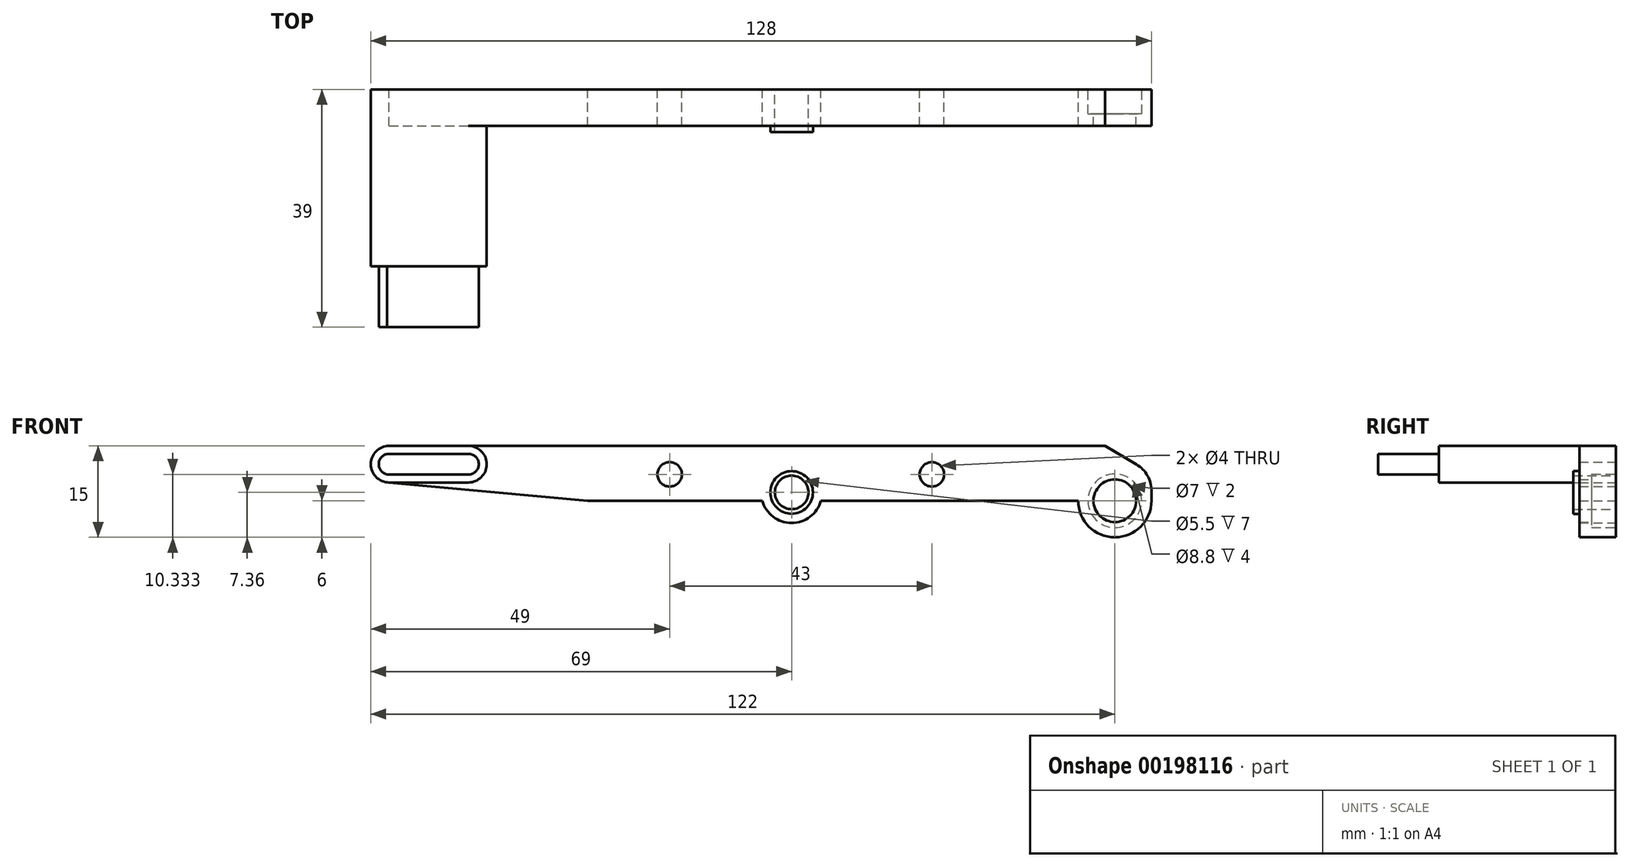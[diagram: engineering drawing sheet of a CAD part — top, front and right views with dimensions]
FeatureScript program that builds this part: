
annotation { "Feature Type Name" : "Feature", "Feature Type Description" : "" }
export const myFeature = defineFeature(function(context is Context, id is Id, definition is map)
    precondition{}
    {
        {
            var Q0;
            Q0=qCreatedBy(makeId("Front.planeOp"),FACE);
            var sketch = newSketch(context, id + "F0", { "sketchPlane" : qUnion([Q0])});
            skLineSegment(sketch, "E0.bottom", {"start": v(32.55, 0) * mm, "end": v(125, 0) * mm});
            skLineSegment(sketch, "E0.top", {"start": v(0, 9) * mm, "end": v(117.37, 9) * mm});
            skLineSegment(sketch, "E0.left", {"start": v(0, 3) * mm, "end": v(0, 9) * mm});
            skLineSegment(sketch, "E0.right", {"start": v(125, 0) * mm, "end": v(125, 1.64) * mm});
            skArc(sketch, "E1", {"start": v(113, 0) * mm, "mid": v(119, -6) * mm, "end": v(125, 0) * mm});
            skCircle(sketch, "E2", {"center": v(119, 0) * mm, "radius": 3.5 * mm});
            skArc(sketch, "E3", {"start": v(61.19, 0) * mm, "mid": v(66, -3.64) * mm, "end": v(70.81, 0) * mm});
            skCircle(sketch, "E4", {"center": v(66, 1.36) * mm, "radius": 2.75 * mm});
            skCircle(sketch, "E5", {"center": v(89, 4.33) * mm, "radius": 2 * mm});
            skCircle(sketch, "E6", {"center": v(46, 4.33) * mm, "radius": 2 * mm});
            skLineSegment(sketch, "E7", {"start": v(117.37, 9) * mm, "end": v(122.54, 5.95) * mm});
            skPoint(sketch, "E8.orphan", {"position": v(125, 9) * mm});
            skLineSegment(sketch, "E9", {"start": v(0, 3) * mm, "end": v(32.55, 0) * mm});
            skPoint(sketch, "E10.orphan", {"position": v(0, 0) * mm});
            skPoint(sketch, "E11.visualSharp", {"position": v(125, 4.5) * mm});
            skArc(sketch, "E11.filletArc", {"start": v(125, 1.64) * mm, "mid": v(124.34, 4.12) * mm, "end": v(122.54, 5.95) * mm});
            skArc(sketch, "E12", {"start": v(0, 9) * mm, "mid": v(-3, 6) * mm, "end": v(0, 3) * mm});
            skSolve(sketch);
        }
        {
            var Q0;
            Q0 = qSketchRegion(id + "F0", true);
            extrude(context, id + "F1", {"entities" : qUnion([Q0]), "depth" : 6 * mm});
        }
        {
            var Q0;
            Q0=makeQuery(id+"F1.opExtrude","CAP_FACE",FACE,{"disambiguationData":[OSD([sQuery(id+"F0.wireOp",EDGE,"E0.bottom"),sQuery(id+"F0.wireOp",EDGE,"E0.top"),sQuery(id+"F0.wireOp",EDGE,"E0.right"),sQuery(id+"F0.wireOp",EDGE,"E1"),sQuery(id+"F0.wireOp",EDGE,"E2"),sQuery(id+"F0.wireOp",EDGE,"E3"),sQuery(id+"F0.wireOp",EDGE,"E4"),sQuery(id+"F0.wireOp",EDGE,"E5"),sQuery(id+"F0.wireOp",EDGE,"E6"),sQuery(id+"F0.wireOp",EDGE,"E7"),sQuery(id+"F0.wireOp",EDGE,"E9"),sQuery(id+"F0.wireOp",EDGE,"E11.filletArc"),sQuery(id+"F0.wireOp",EDGE,"E12")])],"isStart":true});
            var sketch = newSketch(context, id + "F2", { "sketchPlane" : qUnion([Q0])});
            skCircle(sketch, "E13", {"center": v(-119, 0) * mm, "radius": 4.4 * mm});
            skSolve(sketch);
        }
        {
            var Q0;
            Q0 = qSketchRegion(id + "F2", true);
            extrude(context, id + "F3", {"entities" : qUnion([Q0]), "operationType" : NewBodyOperationType.REMOVE, "oppositeDirection" : true, "depth" : 4 * mm});
        }
        {
            var Q0;
            Q0=makeQuery(id+"F1.opExtrude","CAP_FACE",FACE,{"disambiguationData":[OSD([sQuery(id+"F0.wireOp",EDGE,"E0.bottom"),sQuery(id+"F0.wireOp",EDGE,"E0.top"),sQuery(id+"F0.wireOp",EDGE,"E0.right"),sQuery(id+"F0.wireOp",EDGE,"E1"),sQuery(id+"F0.wireOp",EDGE,"E2"),sQuery(id+"F0.wireOp",EDGE,"E3"),sQuery(id+"F0.wireOp",EDGE,"E4"),sQuery(id+"F0.wireOp",EDGE,"E5"),sQuery(id+"F0.wireOp",EDGE,"E6"),sQuery(id+"F0.wireOp",EDGE,"E7"),sQuery(id+"F0.wireOp",EDGE,"E9"),sQuery(id+"F0.wireOp",EDGE,"E11.filletArc"),sQuery(id+"F0.wireOp",EDGE,"E12")])],"isStart":true});
            var sketch = newSketch(context, id + "F4", { "sketchPlane" : qUnion([Q0])});
            skCircle(sketch, "E14", {"center": v(-66, 1.36) * mm, "radius": 2.75 * mm});
            skCircle(sketch, "E15", {"center": v(-66, 1.36) * mm, "radius": 3.5 * mm});
            skSolve(sketch);
        }
        {
            var Q0;
            Q0 = qSketchRegion(id + "F4", true);
            extrude(context, id + "F5", {"entities" : qUnion([Q0]), "operationType" : NewBodyOperationType.ADD, "oppositeDirection" : true, "depth" : 7 * mm});
        }
        {
            var Q0;
            Q0=makeQuery(id+"F1.opExtrude","CAP_FACE",FACE,{"disambiguationData":[OSD([sQuery(id+"F0.wireOp",EDGE,"E0.bottom"),sQuery(id+"F0.wireOp",EDGE,"E0.top"),sQuery(id+"F0.wireOp",EDGE,"E0.right"),sQuery(id+"F0.wireOp",EDGE,"E1"),sQuery(id+"F0.wireOp",EDGE,"E2"),sQuery(id+"F0.wireOp",EDGE,"E3"),sQuery(id+"F0.wireOp",EDGE,"E4"),sQuery(id+"F0.wireOp",EDGE,"E5"),sQuery(id+"F0.wireOp",EDGE,"E6"),sQuery(id+"F0.wireOp",EDGE,"E7"),sQuery(id+"F0.wireOp",EDGE,"E9"),sQuery(id+"F0.wireOp",EDGE,"E11.filletArc"),sQuery(id+"F0.wireOp",EDGE,"E12")])],"isStart":false});
            var sketch = newSketch(context, id + "F6", { "sketchPlane" : qUnion([Q0])});
            skArc(sketch, "E16", {"start": v(0, 9) * mm, "mid": v(-3, 6) * mm, "end": v(0, 3) * mm});
            skLineSegment(sketch, "E17.bottom", {"start": v(0, 3) * mm, "end": v(13, 3) * mm});
            skLineSegment(sketch, "E17.top", {"start": v(0, 9) * mm, "end": v(13, 9) * mm});
            skLineSegment(sketch, "E17.left", {"start": v(0, 3) * mm, "end": v(0, 9) * mm});
            skLineSegment(sketch, "E17.right", {"start": v(13, 3) * mm, "end": v(13, 9) * mm});
            skArc(sketch, "E18", {"start": v(13, 3) * mm, "mid": v(16, 6) * mm, "end": v(13, 9) * mm});
            skSolve(sketch);
        }
        {
            var Q0;
            Q0 = qSketchRegion(id + "F6", true);
            extrude(context, id + "F7", {"entities" : qUnion([Q0]), "operationType" : NewBodyOperationType.ADD, "depth" : 23 * mm});
        }
        {
            var Q0;
            Q0=makeQuery(id+"F7.opExtrude","CAP_FACE",FACE,{"disambiguationData":[OSD([sQuery(id+"F6.wireOp",EDGE,"E16"),sQuery(id+"F6.wireOp",EDGE,"E17.bottom"),sQuery(id+"F6.wireOp",EDGE,"E17.top"),sQuery(id+"F6.wireOp",EDGE,"E18")])],"isStart":false});
            var sketch = newSketch(context, id + "F8", { "sketchPlane" : qUnion([Q0])});
            skArc(sketch, "E19.0", {"start": v(-0.36, 7.66) * mm, "mid": v(-1.7, 6) * mm, "end": v(-0.36, 4.34) * mm});
            skArc(sketch, "E20.0", {"start": v(13, 4.3) * mm, "mid": v(14.7, 6) * mm, "end": v(13, 7.7) * mm});
            skLineSegment(sketch, "E21", {"start": v(-0.36, 7.66) * mm, "end": v(13, 7.7) * mm});
            skLineSegment(sketch, "E22", {"start": v(-0.36, 4.34) * mm, "end": v(13, 4.3) * mm});
            skSolve(sketch);
        }
        {
            var Q0;
            Q0 = qSketchRegion(id + "F8", true);
            extrude(context, id + "F9", {"entities" : qUnion([Q0]), "operationType" : NewBodyOperationType.ADD, "depth" : 10 * mm});
        }
    });
